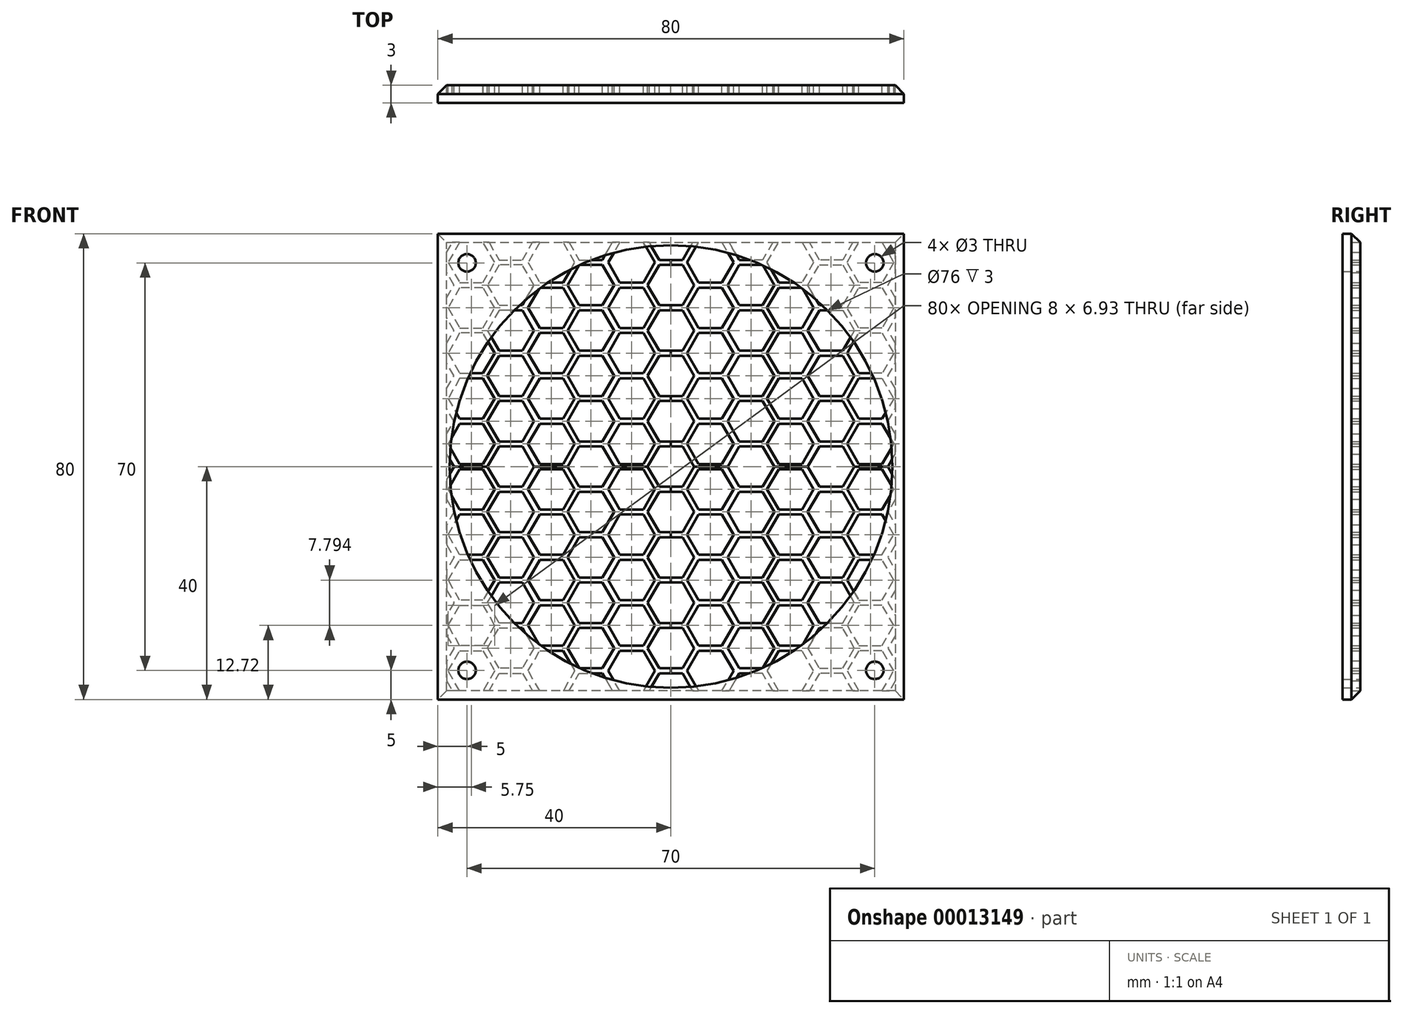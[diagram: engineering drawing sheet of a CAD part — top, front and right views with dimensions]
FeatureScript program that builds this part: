
annotation { "Feature Type Name" : "Feature", "Feature Type Description" : "" }
export const myFeature = defineFeature(function(context is Context, id is Id, definition is map)
    precondition{}
    {
        {
            var Q0;
            Q0=qCreatedBy(makeId("Front.planeOp"),FACE);
            var sketch = newSketch(context, id + "F0", { "sketchPlane" : qUnion([Q0])});
            skLineSegment(sketch, "E0.bottom", {"start": v(-40, 40) * mm, "end": v(40, 40) * mm});
            skLineSegment(sketch, "E0.top", {"start": v(-40, -40) * mm, "end": v(40, -40) * mm});
            skLineSegment(sketch, "E0.left", {"start": v(-40, 40) * mm, "end": v(-40, -40) * mm});
            skLineSegment(sketch, "E0.right", {"start": v(40, 40) * mm, "end": v(40, -40) * mm});
            skCircle(sketch, "E1", {"center": v(0, 0) * mm, "radius": 38 * mm});
            skLineSegment(sketch, "E2.bottom", {"start": v(-35, 35) * mm, "end": v(35, 35) * mm, "construction": true});
            skLineSegment(sketch, "E2.top", {"start": v(-35, -35) * mm, "end": v(35, -35) * mm, "construction": true});
            skLineSegment(sketch, "E2.left", {"start": v(-35, 35) * mm, "end": v(-35, -35) * mm, "construction": true});
            skLineSegment(sketch, "E2.right", {"start": v(35, 35) * mm, "end": v(35, -35) * mm, "construction": true});
            skLineSegment(sketch, "E3", {"start": v(35, 35) * mm, "end": v(-35, -35) * mm, "construction": true});
            skLineSegment(sketch, "E4", {"start": v(-40, 40) * mm, "end": v(40, -40) * mm, "construction": true});
            skCircle(sketch, "E5", {"center": v(35, 35) * mm, "radius": 1.5 * mm});
            skCircle(sketch, "E6", {"center": v(-35, 35) * mm, "radius": 1.5 * mm});
            skCircle(sketch, "E7", {"center": v(35, -35) * mm, "radius": 1.5 * mm});
            skCircle(sketch, "E8", {"center": v(-35, -35) * mm, "radius": 1.5 * mm});
            skSolve(sketch);
        }
        {
            var Q0;
            Q0=makeQuery(id+"F0.imprint","IMPRINT",FACE,{"disambiguationData":[TD([[makeQuery(id+"F0.imprint","IMPRINT",EDGE,{"derivedFrom":sQuery(id+"F0.wireOp",EDGE,"E0.bottom")}),-1.0]])]});
            extrude(context, id + "F1", {"entities" : qUnion([Q0]), "depth" : 3 * mm});
        }
        {
            var Q0;
            Q0=makeQuery(id+"F1.opExtrude","CAP_EDGE",EDGE,{"disambiguationData":[OSD([sQuery(id+"F0.wireOp",EDGE,"E0.bottom")])],"isStart":true});
            var Q1;
            Q1=makeQuery(id+"F1.opExtrude","CAP_EDGE",EDGE,{"disambiguationData":[OSD([sQuery(id+"F0.wireOp",EDGE,"E0.left")])],"isStart":true});
            var Q2;
            Q2=makeQuery(id+"F1.opExtrude","CAP_EDGE",EDGE,{"disambiguationData":[OSD([sQuery(id+"F0.wireOp",EDGE,"E0.top")])],"isStart":true});
            var Q3;
            Q3=makeQuery(id+"F1.opExtrude","CAP_EDGE",EDGE,{"disambiguationData":[OSD([sQuery(id+"F0.wireOp",EDGE,"E0.right")])],"isStart":true});
            chamfer(context, id + "F2", {"entities" : qUnion([Q0, Q1, Q2, Q3]), "width" : 1.5 * mm, "tangentPropagation" : true});
        }
        {
            var Q0;
            Q0=qCreatedBy(makeId("Front.planeOp"),FACE);
            var sketch = newSketch(context, id + "F3", { "sketchPlane" : qUnion([Q0])});
            skCircle(sketch, "E9.cCircle", {"center": v(0, 0) * mm, "radius": 3.46 * mm, "construction": true});
            skLineSegment(sketch, "E9.0", {"start": v(-2, 3.46) * mm, "end": v(2, 3.46) * mm});
            skLineSegment(sketch, "E9.1", {"start": v(2, 3.46) * mm, "end": v(4, 0) * mm});
            skLineSegment(sketch, "E9.2", {"start": v(4, 0) * mm, "end": v(2, -3.46) * mm});
            skLineSegment(sketch, "E9.3", {"start": v(2, -3.46) * mm, "end": v(-2, -3.46) * mm});
            skLineSegment(sketch, "E9.4", {"start": v(-2, -3.46) * mm, "end": v(-4, 0) * mm});
            skLineSegment(sketch, "E9.5", {"start": v(-4, 0) * mm, "end": v(-2, 3.46) * mm});
            skPoint(sketch, "E9.0.midPoint", {"position": v(0, 3.46) * mm});
            skCircle(sketch, "E10.cCircle", {"center": v(6.75, 3.9) * mm, "radius": 3.46 * mm, "construction": true});
            skLineSegment(sketch, "E10.0", {"start": v(4.75, 7.36) * mm, "end": v(8.75, 7.36) * mm});
            skLineSegment(sketch, "E10.1", {"start": v(8.75, 7.36) * mm, "end": v(10.75, 3.9) * mm});
            skLineSegment(sketch, "E10.2", {"start": v(10.75, 3.9) * mm, "end": v(8.75, 0.43) * mm});
            skLineSegment(sketch, "E10.3", {"start": v(8.75, 0.43) * mm, "end": v(4.75, 0.43) * mm});
            skLineSegment(sketch, "E10.4", {"start": v(4.75, 0.43) * mm, "end": v(2.75, 3.9) * mm});
            skLineSegment(sketch, "E10.5", {"start": v(2.75, 3.9) * mm, "end": v(4.75, 7.36) * mm});
            skPoint(sketch, "E10.0.midPoint", {"position": v(6.75, 7.36) * mm});
            skLineSegment(sketch, "E11", {"start": v(0, 0) * mm, "end": v(6.75, 3.9) * mm, "construction": true});
            skLineSegment(sketch, "E12.0.1.0", {"start": v(2, 4.33) * mm, "end": v(-2, 4.33) * mm});
            skLineSegment(sketch, "E12.0.1.1", {"start": v(-2, 4.33) * mm, "end": v(-4, 7.8) * mm});
            skCircle(sketch, "E12.0.1.2", {"center": v(0, 7.8) * mm, "radius": 3.46 * mm, "construction": true});
            skLineSegment(sketch, "E12.0.1.3", {"start": v(4, 7.8) * mm, "end": v(2, 4.33) * mm});
            skLineSegment(sketch, "E12.0.1.4", {"start": v(8.75, 8.23) * mm, "end": v(4.75, 8.23) * mm});
            skLineSegment(sketch, "E12.0.1.5", {"start": v(0, 7.8) * mm, "end": v(6.75, 11.7) * mm, "construction": true});
            skLineSegment(sketch, "E12.0.1.6", {"start": v(-4, 7.8) * mm, "end": v(-2, 11.26) * mm});
            skLineSegment(sketch, "E12.0.1.7", {"start": v(2, 11.26) * mm, "end": v(4, 7.8) * mm});
            skCircle(sketch, "E12.0.1.8", {"center": v(6.75, 11.7) * mm, "radius": 3.46 * mm, "construction": true});
            skPoint(sketch, "E12.0.1.9", {"position": v(0, 11.26) * mm});
            skLineSegment(sketch, "E12.0.1.10", {"start": v(4.75, 8.23) * mm, "end": v(2.75, 11.7) * mm});
            skLineSegment(sketch, "E12.0.1.11", {"start": v(10.75, 11.7) * mm, "end": v(8.75, 8.23) * mm});
            skLineSegment(sketch, "E12.0.1.12", {"start": v(2.75, 11.7) * mm, "end": v(4.75, 15.16) * mm});
            skLineSegment(sketch, "E12.0.1.13", {"start": v(8.75, 15.16) * mm, "end": v(10.75, 11.7) * mm});
            skPoint(sketch, "E12.0.1.14", {"position": v(6.75, 15.16) * mm});
            skLineSegment(sketch, "E12.0.1.15", {"start": v(-2, 11.26) * mm, "end": v(2, 11.26) * mm});
            skLineSegment(sketch, "E12.0.1.16", {"start": v(4.75, 15.16) * mm, "end": v(8.75, 15.16) * mm});
            skLineSegment(sketch, "E12.1.0.0", {"start": v(15.75, -3.46) * mm, "end": v(11.75, -3.46) * mm});
            skLineSegment(sketch, "E12.1.0.1", {"start": v(11.75, -3.46) * mm, "end": v(9.75, 0) * mm});
            skCircle(sketch, "E12.1.0.2", {"center": v(13.75, 0) * mm, "radius": 3.46 * mm, "construction": true});
            skLineSegment(sketch, "E12.1.0.3", {"start": v(17.75, 0) * mm, "end": v(15.75, -3.46) * mm});
            skLineSegment(sketch, "E12.1.0.4", {"start": v(22.5, 0.43) * mm, "end": v(18.5, 0.43) * mm});
            skLineSegment(sketch, "E12.1.0.5", {"start": v(13.75, 0) * mm, "end": v(20.5, 3.9) * mm, "construction": true});
            skLineSegment(sketch, "E12.1.0.6", {"start": v(9.75, 0) * mm, "end": v(11.75, 3.46) * mm});
            skLineSegment(sketch, "E12.1.0.7", {"start": v(15.75, 3.46) * mm, "end": v(17.75, 0) * mm});
            skCircle(sketch, "E12.1.0.8", {"center": v(20.5, 3.9) * mm, "radius": 3.46 * mm, "construction": true});
            skPoint(sketch, "E12.1.0.9", {"position": v(13.75, 3.46) * mm});
            skLineSegment(sketch, "E12.1.0.10", {"start": v(18.5, 0.43) * mm, "end": v(16.5, 3.9) * mm});
            skLineSegment(sketch, "E12.1.0.11", {"start": v(24.5, 3.9) * mm, "end": v(22.5, 0.43) * mm});
            skLineSegment(sketch, "E12.1.0.12", {"start": v(16.5, 3.9) * mm, "end": v(18.5, 7.36) * mm});
            skLineSegment(sketch, "E12.1.0.13", {"start": v(22.5, 7.36) * mm, "end": v(24.5, 3.9) * mm});
            skPoint(sketch, "E12.1.0.14", {"position": v(20.5, 7.36) * mm});
            skLineSegment(sketch, "E12.1.0.15", {"start": v(11.75, 3.46) * mm, "end": v(15.75, 3.46) * mm});
            skLineSegment(sketch, "E12.1.0.16", {"start": v(18.5, 7.36) * mm, "end": v(22.5, 7.36) * mm});
            skLineSegment(sketch, "E12.1.1.0", {"start": v(15.75, 4.33) * mm, "end": v(11.75, 4.33) * mm});
            skLineSegment(sketch, "E12.1.1.1", {"start": v(11.75, 4.33) * mm, "end": v(9.75, 7.8) * mm});
            skCircle(sketch, "E12.1.1.2", {"center": v(13.75, 7.8) * mm, "radius": 3.46 * mm, "construction": true});
            skLineSegment(sketch, "E12.1.1.3", {"start": v(17.75, 7.8) * mm, "end": v(15.75, 4.33) * mm});
            skLineSegment(sketch, "E12.1.1.4", {"start": v(22.5, 8.23) * mm, "end": v(18.5, 8.23) * mm});
            skLineSegment(sketch, "E12.1.1.5", {"start": v(13.75, 7.8) * mm, "end": v(20.5, 11.7) * mm, "construction": true});
            skLineSegment(sketch, "E12.1.1.6", {"start": v(9.75, 7.8) * mm, "end": v(11.75, 11.26) * mm});
            skLineSegment(sketch, "E12.1.1.7", {"start": v(15.75, 11.26) * mm, "end": v(17.75, 7.8) * mm});
            skCircle(sketch, "E12.1.1.8", {"center": v(20.5, 11.7) * mm, "radius": 3.46 * mm, "construction": true});
            skPoint(sketch, "E12.1.1.9", {"position": v(13.75, 11.26) * mm});
            skLineSegment(sketch, "E12.1.1.10", {"start": v(18.5, 8.23) * mm, "end": v(16.5, 11.7) * mm});
            skLineSegment(sketch, "E12.1.1.11", {"start": v(24.5, 11.7) * mm, "end": v(22.5, 8.23) * mm});
            skLineSegment(sketch, "E12.1.1.12", {"start": v(16.5, 11.7) * mm, "end": v(18.5, 15.16) * mm});
            skLineSegment(sketch, "E12.1.1.13", {"start": v(22.5, 15.16) * mm, "end": v(24.5, 11.7) * mm});
            skPoint(sketch, "E12.1.1.14", {"position": v(20.5, 15.16) * mm});
            skLineSegment(sketch, "E12.1.1.15", {"start": v(11.75, 11.26) * mm, "end": v(15.75, 11.26) * mm});
            skLineSegment(sketch, "E12.1.1.16", {"start": v(18.5, 15.16) * mm, "end": v(22.5, 15.16) * mm});
            skLineSegment(sketch, "E12.2.0.0", {"start": v(29.5, -3.46) * mm, "end": v(25.5, -3.46) * mm});
            skLineSegment(sketch, "E12.2.0.1", {"start": v(25.5, -3.46) * mm, "end": v(23.5, 0) * mm});
            skCircle(sketch, "E12.2.0.2", {"center": v(27.5, 0) * mm, "radius": 3.46 * mm, "construction": true});
            skLineSegment(sketch, "E12.2.0.3", {"start": v(31.5, 0) * mm, "end": v(29.5, -3.46) * mm});
            skLineSegment(sketch, "E12.2.0.4", {"start": v(36.25, 0.43) * mm, "end": v(32.25, 0.43) * mm});
            skLineSegment(sketch, "E12.2.0.5", {"start": v(27.5, 0) * mm, "end": v(34.25, 3.9) * mm, "construction": true});
            skLineSegment(sketch, "E12.2.0.6", {"start": v(23.5, 0) * mm, "end": v(25.5, 3.46) * mm});
            skLineSegment(sketch, "E12.2.0.7", {"start": v(29.5, 3.46) * mm, "end": v(31.5, 0) * mm});
            skCircle(sketch, "E12.2.0.8", {"center": v(34.25, 3.9) * mm, "radius": 3.46 * mm, "construction": true});
            skPoint(sketch, "E12.2.0.9", {"position": v(27.5, 3.46) * mm});
            skLineSegment(sketch, "E12.2.0.10", {"start": v(32.25, 0.43) * mm, "end": v(30.25, 3.9) * mm});
            skLineSegment(sketch, "E12.2.0.11", {"start": v(38.25, 3.9) * mm, "end": v(36.25, 0.43) * mm});
            skLineSegment(sketch, "E12.2.0.12", {"start": v(30.25, 3.9) * mm, "end": v(32.25, 7.36) * mm});
            skLineSegment(sketch, "E12.2.0.13", {"start": v(36.25, 7.36) * mm, "end": v(38.25, 3.9) * mm});
            skPoint(sketch, "E12.2.0.14", {"position": v(34.25, 7.36) * mm});
            skLineSegment(sketch, "E12.2.0.15", {"start": v(25.5, 3.46) * mm, "end": v(29.5, 3.46) * mm});
            skLineSegment(sketch, "E12.2.0.16", {"start": v(32.25, 7.36) * mm, "end": v(36.25, 7.36) * mm});
            skLineSegment(sketch, "E12.2.1.0", {"start": v(29.5, 4.33) * mm, "end": v(25.5, 4.33) * mm});
            skLineSegment(sketch, "E12.2.1.1", {"start": v(25.5, 4.33) * mm, "end": v(23.5, 7.8) * mm});
            skCircle(sketch, "E12.2.1.2", {"center": v(27.5, 7.8) * mm, "radius": 3.46 * mm, "construction": true});
            skLineSegment(sketch, "E12.2.1.3", {"start": v(31.5, 7.8) * mm, "end": v(29.5, 4.33) * mm});
            skLineSegment(sketch, "E12.2.1.4", {"start": v(36.25, 8.23) * mm, "end": v(32.25, 8.23) * mm});
            skLineSegment(sketch, "E12.2.1.5", {"start": v(27.5, 7.8) * mm, "end": v(34.25, 11.7) * mm, "construction": true});
            skLineSegment(sketch, "E12.2.1.6", {"start": v(23.5, 7.8) * mm, "end": v(25.5, 11.26) * mm});
            skLineSegment(sketch, "E12.2.1.7", {"start": v(29.5, 11.26) * mm, "end": v(31.5, 7.8) * mm});
            skCircle(sketch, "E12.2.1.8", {"center": v(34.25, 11.7) * mm, "radius": 3.46 * mm, "construction": true});
            skPoint(sketch, "E12.2.1.9", {"position": v(27.5, 11.26) * mm});
            skLineSegment(sketch, "E12.2.1.10", {"start": v(32.25, 8.23) * mm, "end": v(30.25, 11.7) * mm});
            skLineSegment(sketch, "E12.2.1.11", {"start": v(38.25, 11.7) * mm, "end": v(36.25, 8.23) * mm});
            skLineSegment(sketch, "E12.2.1.12", {"start": v(30.25, 11.7) * mm, "end": v(32.25, 15.16) * mm});
            skLineSegment(sketch, "E12.2.1.13", {"start": v(36.25, 15.16) * mm, "end": v(38.25, 11.7) * mm});
            skPoint(sketch, "E12.2.1.14", {"position": v(34.25, 15.16) * mm});
            skLineSegment(sketch, "E12.2.1.15", {"start": v(25.5, 11.26) * mm, "end": v(29.5, 11.26) * mm});
            skLineSegment(sketch, "E12.2.1.16", {"start": v(32.25, 15.16) * mm, "end": v(36.25, 15.16) * mm});
            skLineSegment(sketch, "E12.direction1", {"start": v(-2, -3.46) * mm, "end": v(11.75, -3.46) * mm, "construction": true});
            skLineSegment(sketch, "E12.direction2", {"start": v(-2, -3.46) * mm, "end": v(-2, 4.33) * mm, "construction": true});
            skLineSegment(sketch, "E13", {"start": v(0, 35) * mm, "end": v(0, 0) * mm});
            skLineSegment(sketch, "E14.0.0.2", {"start": v(2, 12.12) * mm, "end": v(-2, 12.12) * mm});
            skLineSegment(sketch, "E14.3.0.2", {"start": v(-2, 12.12) * mm, "end": v(-4, 15.59) * mm});
            skCircle(sketch, "E14.6.0.2", {"center": v(0, 15.59) * mm, "radius": 3.46 * mm, "construction": true});
            skLineSegment(sketch, "E14.8.0.2", {"start": v(4, 15.59) * mm, "end": v(2, 12.12) * mm});
            skLineSegment(sketch, "E14.11.0.2", {"start": v(8.75, 16.02) * mm, "end": v(4.75, 16.02) * mm});
            skLineSegment(sketch, "E14.14.0.2", {"start": v(0, 15.59) * mm, "end": v(6.75, 19.49) * mm, "construction": true});
            skLineSegment(sketch, "E14.17.0.2", {"start": v(-4, 15.59) * mm, "end": v(-2, 19.05) * mm});
            skLineSegment(sketch, "E14.20.0.2", {"start": v(2, 19.05) * mm, "end": v(4, 15.59) * mm});
            skCircle(sketch, "E14.23.0.2", {"center": v(6.75, 19.49) * mm, "radius": 3.46 * mm, "construction": true});
            skPoint(sketch, "E14.25.0.2", {"position": v(0, 19.05) * mm});
            skLineSegment(sketch, "E14.26.0.2", {"start": v(4.75, 16.02) * mm, "end": v(2.75, 19.49) * mm});
            skLineSegment(sketch, "E14.29.0.2", {"start": v(10.75, 19.49) * mm, "end": v(8.75, 16.02) * mm});
            skLineSegment(sketch, "E14.32.0.2", {"start": v(2.75, 19.49) * mm, "end": v(4.75, 22.95) * mm});
            skLineSegment(sketch, "E14.35.0.2", {"start": v(8.75, 22.95) * mm, "end": v(10.75, 19.49) * mm});
            skPoint(sketch, "E14.38.0.2", {"position": v(6.75, 22.95) * mm});
            skLineSegment(sketch, "E14.39.0.2", {"start": v(-2, 19.05) * mm, "end": v(2, 19.05) * mm});
            skLineSegment(sketch, "E14.42.0.2", {"start": v(4.75, 22.95) * mm, "end": v(8.75, 22.95) * mm});
            skLineSegment(sketch, "E14.0.0.3", {"start": v(2, 19.92) * mm, "end": v(-2, 19.92) * mm});
            skLineSegment(sketch, "E14.3.0.3", {"start": v(-2, 19.92) * mm, "end": v(-4, 23.38) * mm});
            skCircle(sketch, "E14.6.0.3", {"center": v(0, 23.38) * mm, "radius": 3.46 * mm, "construction": true});
            skLineSegment(sketch, "E14.8.0.3", {"start": v(4, 23.38) * mm, "end": v(2, 19.92) * mm});
            skLineSegment(sketch, "E14.11.0.3", {"start": v(8.75, 23.82) * mm, "end": v(4.75, 23.82) * mm});
            skLineSegment(sketch, "E14.14.0.3", {"start": v(0, 23.38) * mm, "end": v(6.75, 27.28) * mm, "construction": true});
            skLineSegment(sketch, "E14.17.0.3", {"start": v(-4, 23.38) * mm, "end": v(-2, 26.85) * mm});
            skLineSegment(sketch, "E14.20.0.3", {"start": v(2, 26.85) * mm, "end": v(4, 23.38) * mm});
            skCircle(sketch, "E14.23.0.3", {"center": v(6.75, 27.28) * mm, "radius": 3.46 * mm, "construction": true});
            skPoint(sketch, "E14.25.0.3", {"position": v(0, 26.85) * mm});
            skLineSegment(sketch, "E14.26.0.3", {"start": v(4.75, 23.82) * mm, "end": v(2.75, 27.28) * mm});
            skLineSegment(sketch, "E14.29.0.3", {"start": v(10.75, 27.28) * mm, "end": v(8.75, 23.82) * mm});
            skLineSegment(sketch, "E14.32.0.3", {"start": v(2.75, 27.28) * mm, "end": v(4.75, 30.74) * mm});
            skLineSegment(sketch, "E14.35.0.3", {"start": v(8.75, 30.74) * mm, "end": v(10.75, 27.28) * mm});
            skPoint(sketch, "E14.38.0.3", {"position": v(6.75, 30.74) * mm});
            skLineSegment(sketch, "E14.39.0.3", {"start": v(-2, 26.85) * mm, "end": v(2, 26.85) * mm});
            skLineSegment(sketch, "E14.42.0.3", {"start": v(4.75, 30.74) * mm, "end": v(8.75, 30.74) * mm});
            skLineSegment(sketch, "E14.0.1.2", {"start": v(15.75, 12.12) * mm, "end": v(11.75, 12.12) * mm});
            skLineSegment(sketch, "E14.3.1.2", {"start": v(11.75, 12.12) * mm, "end": v(9.75, 15.59) * mm});
            skCircle(sketch, "E14.6.1.2", {"center": v(13.75, 15.59) * mm, "radius": 3.46 * mm, "construction": true});
            skLineSegment(sketch, "E14.8.1.2", {"start": v(17.75, 15.59) * mm, "end": v(15.75, 12.12) * mm});
            skLineSegment(sketch, "E14.11.1.2", {"start": v(22.5, 16.02) * mm, "end": v(18.5, 16.02) * mm});
            skLineSegment(sketch, "E14.14.1.2", {"start": v(13.75, 15.59) * mm, "end": v(20.5, 19.49) * mm, "construction": true});
            skLineSegment(sketch, "E14.17.1.2", {"start": v(9.75, 15.59) * mm, "end": v(11.75, 19.05) * mm});
            skLineSegment(sketch, "E14.20.1.2", {"start": v(15.75, 19.05) * mm, "end": v(17.75, 15.59) * mm});
            skCircle(sketch, "E14.23.1.2", {"center": v(20.5, 19.49) * mm, "radius": 3.46 * mm, "construction": true});
            skPoint(sketch, "E14.25.1.2", {"position": v(13.75, 19.05) * mm});
            skLineSegment(sketch, "E14.26.1.2", {"start": v(18.5, 16.02) * mm, "end": v(16.5, 19.49) * mm});
            skLineSegment(sketch, "E14.29.1.2", {"start": v(24.5, 19.49) * mm, "end": v(22.5, 16.02) * mm});
            skLineSegment(sketch, "E14.32.1.2", {"start": v(16.5, 19.49) * mm, "end": v(18.5, 22.95) * mm});
            skLineSegment(sketch, "E14.35.1.2", {"start": v(22.5, 22.95) * mm, "end": v(24.5, 19.49) * mm});
            skPoint(sketch, "E14.38.1.2", {"position": v(20.5, 22.95) * mm});
            skLineSegment(sketch, "E14.39.1.2", {"start": v(11.75, 19.05) * mm, "end": v(15.75, 19.05) * mm});
            skLineSegment(sketch, "E14.42.1.2", {"start": v(18.5, 22.95) * mm, "end": v(22.5, 22.95) * mm});
            skLineSegment(sketch, "E14.0.1.3", {"start": v(15.75, 19.92) * mm, "end": v(11.75, 19.92) * mm});
            skLineSegment(sketch, "E14.3.1.3", {"start": v(11.75, 19.92) * mm, "end": v(9.75, 23.38) * mm});
            skCircle(sketch, "E14.6.1.3", {"center": v(13.75, 23.38) * mm, "radius": 3.46 * mm, "construction": true});
            skLineSegment(sketch, "E14.8.1.3", {"start": v(17.75, 23.38) * mm, "end": v(15.75, 19.92) * mm});
            skLineSegment(sketch, "E14.11.1.3", {"start": v(22.5, 23.82) * mm, "end": v(18.5, 23.82) * mm});
            skLineSegment(sketch, "E14.14.1.3", {"start": v(13.75, 23.38) * mm, "end": v(20.5, 27.28) * mm, "construction": true});
            skLineSegment(sketch, "E14.17.1.3", {"start": v(9.75, 23.38) * mm, "end": v(11.75, 26.85) * mm});
            skLineSegment(sketch, "E14.20.1.3", {"start": v(15.75, 26.85) * mm, "end": v(17.75, 23.38) * mm});
            skCircle(sketch, "E14.23.1.3", {"center": v(20.5, 27.28) * mm, "radius": 3.46 * mm, "construction": true});
            skPoint(sketch, "E14.25.1.3", {"position": v(13.75, 26.85) * mm});
            skLineSegment(sketch, "E14.26.1.3", {"start": v(18.5, 23.82) * mm, "end": v(16.5, 27.28) * mm});
            skLineSegment(sketch, "E14.29.1.3", {"start": v(24.5, 27.28) * mm, "end": v(22.5, 23.82) * mm});
            skLineSegment(sketch, "E14.32.1.3", {"start": v(16.5, 27.28) * mm, "end": v(18.5, 30.74) * mm});
            skLineSegment(sketch, "E14.35.1.3", {"start": v(22.5, 30.74) * mm, "end": v(24.5, 27.28) * mm});
            skPoint(sketch, "E14.38.1.3", {"position": v(20.5, 30.74) * mm});
            skLineSegment(sketch, "E14.39.1.3", {"start": v(11.75, 26.85) * mm, "end": v(15.75, 26.85) * mm});
            skLineSegment(sketch, "E14.42.1.3", {"start": v(18.5, 30.74) * mm, "end": v(22.5, 30.74) * mm});
            skLineSegment(sketch, "E14.0.2.2", {"start": v(29.5, 12.12) * mm, "end": v(25.5, 12.12) * mm});
            skLineSegment(sketch, "E14.3.2.2", {"start": v(25.5, 12.12) * mm, "end": v(23.5, 15.59) * mm});
            skCircle(sketch, "E14.6.2.2", {"center": v(27.5, 15.59) * mm, "radius": 3.46 * mm, "construction": true});
            skLineSegment(sketch, "E14.8.2.2", {"start": v(31.5, 15.59) * mm, "end": v(29.5, 12.12) * mm});
            skLineSegment(sketch, "E14.11.2.2", {"start": v(36.25, 16.02) * mm, "end": v(32.25, 16.02) * mm});
            skLineSegment(sketch, "E14.14.2.2", {"start": v(27.5, 15.59) * mm, "end": v(34.25, 19.49) * mm, "construction": true});
            skLineSegment(sketch, "E14.17.2.2", {"start": v(23.5, 15.59) * mm, "end": v(25.5, 19.05) * mm});
            skLineSegment(sketch, "E14.20.2.2", {"start": v(29.5, 19.05) * mm, "end": v(31.5, 15.59) * mm});
            skCircle(sketch, "E14.23.2.2", {"center": v(34.25, 19.49) * mm, "radius": 3.46 * mm, "construction": true});
            skPoint(sketch, "E14.25.2.2", {"position": v(27.5, 19.05) * mm});
            skLineSegment(sketch, "E14.26.2.2", {"start": v(32.25, 16.02) * mm, "end": v(30.25, 19.49) * mm});
            skLineSegment(sketch, "E14.29.2.2", {"start": v(38.25, 19.49) * mm, "end": v(36.25, 16.02) * mm});
            skLineSegment(sketch, "E14.32.2.2", {"start": v(30.25, 19.49) * mm, "end": v(32.25, 22.95) * mm});
            skLineSegment(sketch, "E14.35.2.2", {"start": v(36.25, 22.95) * mm, "end": v(38.25, 19.49) * mm});
            skPoint(sketch, "E14.38.2.2", {"position": v(34.25, 22.95) * mm});
            skLineSegment(sketch, "E14.39.2.2", {"start": v(25.5, 19.05) * mm, "end": v(29.5, 19.05) * mm});
            skLineSegment(sketch, "E14.42.2.2", {"start": v(32.25, 22.95) * mm, "end": v(36.25, 22.95) * mm});
            skLineSegment(sketch, "E14.0.2.3", {"start": v(29.5, 19.92) * mm, "end": v(25.5, 19.92) * mm});
            skLineSegment(sketch, "E14.3.2.3", {"start": v(25.5, 19.92) * mm, "end": v(23.5, 23.38) * mm});
            skCircle(sketch, "E14.6.2.3", {"center": v(27.5, 23.38) * mm, "radius": 3.46 * mm, "construction": true});
            skLineSegment(sketch, "E14.8.2.3", {"start": v(31.5, 23.38) * mm, "end": v(29.5, 19.92) * mm});
            skLineSegment(sketch, "E14.11.2.3", {"start": v(36.25, 23.82) * mm, "end": v(32.25, 23.82) * mm});
            skLineSegment(sketch, "E14.14.2.3", {"start": v(27.5, 23.38) * mm, "end": v(34.25, 27.28) * mm, "construction": true});
            skLineSegment(sketch, "E14.17.2.3", {"start": v(23.5, 23.38) * mm, "end": v(25.5, 26.85) * mm});
            skLineSegment(sketch, "E14.20.2.3", {"start": v(29.5, 26.85) * mm, "end": v(31.5, 23.38) * mm});
            skCircle(sketch, "E14.23.2.3", {"center": v(34.25, 27.28) * mm, "radius": 3.46 * mm, "construction": true});
            skPoint(sketch, "E14.25.2.3", {"position": v(27.5, 26.85) * mm});
            skLineSegment(sketch, "E14.26.2.3", {"start": v(32.25, 23.82) * mm, "end": v(30.25, 27.28) * mm});
            skLineSegment(sketch, "E14.29.2.3", {"start": v(38.25, 27.28) * mm, "end": v(36.25, 23.82) * mm});
            skLineSegment(sketch, "E14.32.2.3", {"start": v(30.25, 27.28) * mm, "end": v(32.25, 30.74) * mm});
            skLineSegment(sketch, "E14.35.2.3", {"start": v(36.25, 30.74) * mm, "end": v(38.25, 27.28) * mm});
            skPoint(sketch, "E14.38.2.3", {"position": v(34.25, 30.74) * mm});
            skLineSegment(sketch, "E14.39.2.3", {"start": v(25.5, 26.85) * mm, "end": v(29.5, 26.85) * mm});
            skLineSegment(sketch, "E14.42.2.3", {"start": v(32.25, 30.74) * mm, "end": v(36.25, 30.74) * mm});
            skLineSegment(sketch, "E15.0.0.4", {"start": v(2, 27.71) * mm, "end": v(-2, 27.71) * mm});
            skLineSegment(sketch, "E15.3.0.4", {"start": v(-2, 27.71) * mm, "end": v(-4, 31.18) * mm});
            skCircle(sketch, "E15.6.0.4", {"center": v(0, 31.18) * mm, "radius": 3.46 * mm, "construction": true});
            skLineSegment(sketch, "E15.8.0.4", {"start": v(4, 31.18) * mm, "end": v(2, 27.71) * mm});
            skLineSegment(sketch, "E15.11.0.4", {"start": v(8.75, 31.6) * mm, "end": v(4.75, 31.6) * mm});
            skLineSegment(sketch, "E15.14.0.4", {"start": v(0, 31.18) * mm, "end": v(6.75, 35.07) * mm, "construction": true});
            skLineSegment(sketch, "E15.17.0.4", {"start": v(-4, 31.18) * mm, "end": v(-2, 34.64) * mm});
            skLineSegment(sketch, "E15.20.0.4", {"start": v(2, 34.64) * mm, "end": v(4, 31.18) * mm});
            skCircle(sketch, "E15.23.0.4", {"center": v(6.75, 35.07) * mm, "radius": 3.46 * mm, "construction": true});
            skPoint(sketch, "E15.25.0.4", {"position": v(0, 34.64) * mm});
            skLineSegment(sketch, "E15.26.0.4", {"start": v(4.75, 31.6) * mm, "end": v(2.75, 35.07) * mm});
            skLineSegment(sketch, "E15.29.0.4", {"start": v(10.75, 35.07) * mm, "end": v(8.75, 31.6) * mm});
            skLineSegment(sketch, "E15.32.0.4", {"start": v(2.75, 35.07) * mm, "end": v(4.75, 38.54) * mm});
            skLineSegment(sketch, "E15.35.0.4", {"start": v(8.75, 38.54) * mm, "end": v(10.75, 35.07) * mm});
            skPoint(sketch, "E15.38.0.4", {"position": v(6.75, 38.54) * mm});
            skLineSegment(sketch, "E15.39.0.4", {"start": v(-2, 34.64) * mm, "end": v(2, 34.64) * mm});
            skLineSegment(sketch, "E15.42.0.4", {"start": v(4.75, 38.54) * mm, "end": v(8.75, 38.54) * mm});
            skLineSegment(sketch, "E15.0.1.4", {"start": v(15.75, 27.71) * mm, "end": v(11.75, 27.71) * mm});
            skLineSegment(sketch, "E15.3.1.4", {"start": v(11.75, 27.71) * mm, "end": v(9.75, 31.18) * mm});
            skCircle(sketch, "E15.6.1.4", {"center": v(13.75, 31.18) * mm, "radius": 3.46 * mm, "construction": true});
            skLineSegment(sketch, "E15.8.1.4", {"start": v(17.75, 31.18) * mm, "end": v(15.75, 27.71) * mm});
            skLineSegment(sketch, "E15.11.1.4", {"start": v(22.5, 31.6) * mm, "end": v(18.5, 31.6) * mm});
            skLineSegment(sketch, "E15.14.1.4", {"start": v(13.75, 31.18) * mm, "end": v(20.5, 35.07) * mm, "construction": true});
            skLineSegment(sketch, "E15.17.1.4", {"start": v(9.75, 31.18) * mm, "end": v(11.75, 34.64) * mm});
            skLineSegment(sketch, "E15.20.1.4", {"start": v(15.75, 34.64) * mm, "end": v(17.75, 31.18) * mm});
            skCircle(sketch, "E15.23.1.4", {"center": v(20.5, 35.07) * mm, "radius": 3.46 * mm, "construction": true});
            skPoint(sketch, "E15.25.1.4", {"position": v(13.75, 34.64) * mm});
            skLineSegment(sketch, "E15.26.1.4", {"start": v(18.5, 31.6) * mm, "end": v(16.5, 35.07) * mm});
            skLineSegment(sketch, "E15.29.1.4", {"start": v(24.5, 35.07) * mm, "end": v(22.5, 31.6) * mm});
            skLineSegment(sketch, "E15.32.1.4", {"start": v(16.5, 35.07) * mm, "end": v(18.5, 38.54) * mm});
            skLineSegment(sketch, "E15.35.1.4", {"start": v(22.5, 38.54) * mm, "end": v(24.5, 35.07) * mm});
            skPoint(sketch, "E15.38.1.4", {"position": v(20.5, 38.54) * mm});
            skLineSegment(sketch, "E15.39.1.4", {"start": v(11.75, 34.64) * mm, "end": v(15.75, 34.64) * mm});
            skLineSegment(sketch, "E15.42.1.4", {"start": v(18.5, 38.54) * mm, "end": v(22.5, 38.54) * mm});
            skLineSegment(sketch, "E15.0.2.4", {"start": v(29.5, 27.71) * mm, "end": v(25.5, 27.71) * mm});
            skLineSegment(sketch, "E15.3.2.4", {"start": v(25.5, 27.71) * mm, "end": v(23.5, 31.18) * mm});
            skCircle(sketch, "E15.6.2.4", {"center": v(27.5, 31.18) * mm, "radius": 3.46 * mm, "construction": true});
            skLineSegment(sketch, "E15.8.2.4", {"start": v(31.5, 31.18) * mm, "end": v(29.5, 27.71) * mm});
            skLineSegment(sketch, "E15.11.2.4", {"start": v(36.25, 31.6) * mm, "end": v(32.25, 31.6) * mm});
            skLineSegment(sketch, "E15.14.2.4", {"start": v(27.5, 31.18) * mm, "end": v(34.25, 35.07) * mm, "construction": true});
            skLineSegment(sketch, "E15.17.2.4", {"start": v(23.5, 31.18) * mm, "end": v(25.5, 34.64) * mm});
            skLineSegment(sketch, "E15.20.2.4", {"start": v(29.5, 34.64) * mm, "end": v(31.5, 31.18) * mm});
            skCircle(sketch, "E15.23.2.4", {"center": v(34.25, 35.07) * mm, "radius": 3.46 * mm, "construction": true});
            skPoint(sketch, "E15.25.2.4", {"position": v(27.5, 34.64) * mm});
            skLineSegment(sketch, "E15.26.2.4", {"start": v(32.25, 31.6) * mm, "end": v(30.25, 35.07) * mm});
            skLineSegment(sketch, "E15.29.2.4", {"start": v(38.25, 35.07) * mm, "end": v(36.25, 31.6) * mm});
            skLineSegment(sketch, "E15.32.2.4", {"start": v(30.25, 35.07) * mm, "end": v(32.25, 38.54) * mm});
            skLineSegment(sketch, "E15.35.2.4", {"start": v(36.25, 38.54) * mm, "end": v(38.25, 35.07) * mm});
            skPoint(sketch, "E15.38.2.4", {"position": v(34.25, 38.54) * mm});
            skLineSegment(sketch, "E15.39.2.4", {"start": v(25.5, 34.64) * mm, "end": v(29.5, 34.64) * mm});
            skLineSegment(sketch, "E15.42.2.4", {"start": v(32.25, 38.54) * mm, "end": v(36.25, 38.54) * mm});
            skLineSegment(sketch, "E16.bottom", {"start": v(0, 0) * mm, "end": v(38.5, 0) * mm});
            skLineSegment(sketch, "E16.top", {"start": v(0, 38.5) * mm, "end": v(38.5, 38.5) * mm});
            skLineSegment(sketch, "E16.left", {"start": v(0, 0) * mm, "end": v(0, 38.5) * mm});
            skLineSegment(sketch, "E16.right", {"start": v(38.5, 0) * mm, "end": v(38.5, 38.5) * mm});
            skLineSegment(sketch, "E17.0.3.0", {"start": v(43.25, -3.46) * mm, "end": v(39.25, -3.46) * mm});
            skLineSegment(sketch, "E17.3.3.0", {"start": v(39.25, -3.46) * mm, "end": v(37.25, 0) * mm});
            skCircle(sketch, "E17.6.3.0", {"center": v(41.25, 0) * mm, "radius": 3.46 * mm, "construction": true});
            skLineSegment(sketch, "E17.8.3.0", {"start": v(45.25, 0) * mm, "end": v(43.25, -3.46) * mm});
            skLineSegment(sketch, "E17.11.3.0", {"start": v(50, 0.43) * mm, "end": v(46, 0.43) * mm});
            skLineSegment(sketch, "E17.14.3.0", {"start": v(41.25, 0) * mm, "end": v(48, 3.9) * mm, "construction": true});
            skLineSegment(sketch, "E17.17.3.0", {"start": v(37.25, 0) * mm, "end": v(39.25, 3.46) * mm});
            skLineSegment(sketch, "E17.20.3.0", {"start": v(43.25, 3.46) * mm, "end": v(45.25, 0) * mm});
            skCircle(sketch, "E17.23.3.0", {"center": v(48, 3.9) * mm, "radius": 3.46 * mm, "construction": true});
            skPoint(sketch, "E17.25.3.0", {"position": v(41.25, 3.46) * mm});
            skLineSegment(sketch, "E17.26.3.0", {"start": v(46, 0.43) * mm, "end": v(44, 3.9) * mm});
            skLineSegment(sketch, "E17.29.3.0", {"start": v(52, 3.9) * mm, "end": v(50, 0.43) * mm});
            skLineSegment(sketch, "E17.32.3.0", {"start": v(44, 3.9) * mm, "end": v(46, 7.36) * mm});
            skLineSegment(sketch, "E17.35.3.0", {"start": v(50, 7.36) * mm, "end": v(52, 3.9) * mm});
            skPoint(sketch, "E17.38.3.0", {"position": v(48, 7.36) * mm});
            skLineSegment(sketch, "E17.39.3.0", {"start": v(39.25, 3.46) * mm, "end": v(43.25, 3.46) * mm});
            skLineSegment(sketch, "E17.42.3.0", {"start": v(46, 7.36) * mm, "end": v(50, 7.36) * mm});
            skLineSegment(sketch, "E17.0.3.1", {"start": v(43.25, 4.33) * mm, "end": v(39.25, 4.33) * mm});
            skLineSegment(sketch, "E17.3.3.1", {"start": v(39.25, 4.33) * mm, "end": v(37.25, 7.8) * mm});
            skCircle(sketch, "E17.6.3.1", {"center": v(41.25, 7.8) * mm, "radius": 3.46 * mm, "construction": true});
            skLineSegment(sketch, "E17.8.3.1", {"start": v(45.25, 7.8) * mm, "end": v(43.25, 4.33) * mm});
            skLineSegment(sketch, "E17.11.3.1", {"start": v(50, 8.23) * mm, "end": v(46, 8.23) * mm});
            skLineSegment(sketch, "E17.14.3.1", {"start": v(41.25, 7.8) * mm, "end": v(48, 11.7) * mm, "construction": true});
            skLineSegment(sketch, "E17.17.3.1", {"start": v(37.25, 7.8) * mm, "end": v(39.25, 11.26) * mm});
            skLineSegment(sketch, "E17.20.3.1", {"start": v(43.25, 11.26) * mm, "end": v(45.25, 7.8) * mm});
            skCircle(sketch, "E17.23.3.1", {"center": v(48, 11.7) * mm, "radius": 3.46 * mm, "construction": true});
            skPoint(sketch, "E17.25.3.1", {"position": v(41.25, 11.26) * mm});
            skLineSegment(sketch, "E17.26.3.1", {"start": v(46, 8.23) * mm, "end": v(44, 11.7) * mm});
            skLineSegment(sketch, "E17.29.3.1", {"start": v(52, 11.7) * mm, "end": v(50, 8.23) * mm});
            skLineSegment(sketch, "E17.32.3.1", {"start": v(44, 11.7) * mm, "end": v(46, 15.16) * mm});
            skLineSegment(sketch, "E17.35.3.1", {"start": v(50, 15.16) * mm, "end": v(52, 11.7) * mm});
            skPoint(sketch, "E17.38.3.1", {"position": v(48, 15.16) * mm});
            skLineSegment(sketch, "E17.39.3.1", {"start": v(39.25, 11.26) * mm, "end": v(43.25, 11.26) * mm});
            skLineSegment(sketch, "E17.42.3.1", {"start": v(46, 15.16) * mm, "end": v(50, 15.16) * mm});
            skLineSegment(sketch, "E17.0.3.2", {"start": v(43.25, 12.12) * mm, "end": v(39.25, 12.12) * mm});
            skLineSegment(sketch, "E17.3.3.2", {"start": v(39.25, 12.12) * mm, "end": v(37.25, 15.59) * mm});
            skCircle(sketch, "E17.6.3.2", {"center": v(41.25, 15.59) * mm, "radius": 3.46 * mm, "construction": true});
            skLineSegment(sketch, "E17.8.3.2", {"start": v(45.25, 15.59) * mm, "end": v(43.25, 12.12) * mm});
            skLineSegment(sketch, "E17.11.3.2", {"start": v(50, 16.02) * mm, "end": v(46, 16.02) * mm});
            skLineSegment(sketch, "E17.14.3.2", {"start": v(41.25, 15.59) * mm, "end": v(48, 19.49) * mm, "construction": true});
            skLineSegment(sketch, "E17.17.3.2", {"start": v(37.25, 15.59) * mm, "end": v(39.25, 19.05) * mm});
            skLineSegment(sketch, "E17.20.3.2", {"start": v(43.25, 19.05) * mm, "end": v(45.25, 15.59) * mm});
            skCircle(sketch, "E17.23.3.2", {"center": v(48, 19.49) * mm, "radius": 3.46 * mm, "construction": true});
            skPoint(sketch, "E17.25.3.2", {"position": v(41.25, 19.05) * mm});
            skLineSegment(sketch, "E17.26.3.2", {"start": v(46, 16.02) * mm, "end": v(44, 19.49) * mm});
            skLineSegment(sketch, "E17.29.3.2", {"start": v(52, 19.49) * mm, "end": v(50, 16.02) * mm});
            skLineSegment(sketch, "E17.32.3.2", {"start": v(44, 19.49) * mm, "end": v(46, 22.95) * mm});
            skLineSegment(sketch, "E17.35.3.2", {"start": v(50, 22.95) * mm, "end": v(52, 19.49) * mm});
            skPoint(sketch, "E17.38.3.2", {"position": v(48, 22.95) * mm});
            skLineSegment(sketch, "E17.39.3.2", {"start": v(39.25, 19.05) * mm, "end": v(43.25, 19.05) * mm});
            skLineSegment(sketch, "E17.42.3.2", {"start": v(46, 22.95) * mm, "end": v(50, 22.95) * mm});
            skLineSegment(sketch, "E17.0.3.3", {"start": v(43.25, 19.92) * mm, "end": v(39.25, 19.92) * mm});
            skLineSegment(sketch, "E17.3.3.3", {"start": v(39.25, 19.92) * mm, "end": v(37.25, 23.38) * mm});
            skCircle(sketch, "E17.6.3.3", {"center": v(41.25, 23.38) * mm, "radius": 3.46 * mm, "construction": true});
            skLineSegment(sketch, "E17.8.3.3", {"start": v(45.25, 23.38) * mm, "end": v(43.25, 19.92) * mm});
            skLineSegment(sketch, "E17.11.3.3", {"start": v(50, 23.82) * mm, "end": v(46, 23.82) * mm});
            skLineSegment(sketch, "E17.14.3.3", {"start": v(41.25, 23.38) * mm, "end": v(48, 27.28) * mm, "construction": true});
            skLineSegment(sketch, "E17.17.3.3", {"start": v(37.25, 23.38) * mm, "end": v(39.25, 26.85) * mm});
            skLineSegment(sketch, "E17.20.3.3", {"start": v(43.25, 26.85) * mm, "end": v(45.25, 23.38) * mm});
            skCircle(sketch, "E17.23.3.3", {"center": v(48, 27.28) * mm, "radius": 3.46 * mm, "construction": true});
            skPoint(sketch, "E17.25.3.3", {"position": v(41.25, 26.85) * mm});
            skLineSegment(sketch, "E17.26.3.3", {"start": v(46, 23.82) * mm, "end": v(44, 27.28) * mm});
            skLineSegment(sketch, "E17.29.3.3", {"start": v(52, 27.28) * mm, "end": v(50, 23.82) * mm});
            skLineSegment(sketch, "E17.32.3.3", {"start": v(44, 27.28) * mm, "end": v(46, 30.74) * mm});
            skLineSegment(sketch, "E17.35.3.3", {"start": v(50, 30.74) * mm, "end": v(52, 27.28) * mm});
            skPoint(sketch, "E17.38.3.3", {"position": v(48, 30.74) * mm});
            skLineSegment(sketch, "E17.39.3.3", {"start": v(39.25, 26.85) * mm, "end": v(43.25, 26.85) * mm});
            skLineSegment(sketch, "E17.42.3.3", {"start": v(46, 30.74) * mm, "end": v(50, 30.74) * mm});
            skLineSegment(sketch, "E17.0.3.4", {"start": v(43.25, 27.71) * mm, "end": v(39.25, 27.71) * mm});
            skLineSegment(sketch, "E17.3.3.4", {"start": v(39.25, 27.71) * mm, "end": v(37.25, 31.18) * mm});
            skCircle(sketch, "E17.6.3.4", {"center": v(41.25, 31.18) * mm, "radius": 3.46 * mm, "construction": true});
            skLineSegment(sketch, "E17.8.3.4", {"start": v(45.25, 31.18) * mm, "end": v(43.25, 27.71) * mm});
            skLineSegment(sketch, "E17.11.3.4", {"start": v(50, 31.6) * mm, "end": v(46, 31.6) * mm});
            skLineSegment(sketch, "E17.14.3.4", {"start": v(41.25, 31.18) * mm, "end": v(48, 35.07) * mm, "construction": true});
            skLineSegment(sketch, "E17.17.3.4", {"start": v(37.25, 31.18) * mm, "end": v(39.25, 34.64) * mm});
            skLineSegment(sketch, "E17.20.3.4", {"start": v(43.25, 34.64) * mm, "end": v(45.25, 31.18) * mm});
            skCircle(sketch, "E17.23.3.4", {"center": v(48, 35.07) * mm, "radius": 3.46 * mm, "construction": true});
            skPoint(sketch, "E17.25.3.4", {"position": v(41.25, 34.64) * mm});
            skLineSegment(sketch, "E17.26.3.4", {"start": v(46, 31.6) * mm, "end": v(44, 35.07) * mm});
            skLineSegment(sketch, "E17.29.3.4", {"start": v(52, 35.07) * mm, "end": v(50, 31.6) * mm});
            skLineSegment(sketch, "E17.32.3.4", {"start": v(44, 35.07) * mm, "end": v(46, 38.54) * mm});
            skLineSegment(sketch, "E17.35.3.4", {"start": v(50, 38.54) * mm, "end": v(52, 35.07) * mm});
            skPoint(sketch, "E17.38.3.4", {"position": v(48, 38.54) * mm});
            skLineSegment(sketch, "E17.39.3.4", {"start": v(39.25, 34.64) * mm, "end": v(43.25, 34.64) * mm});
            skLineSegment(sketch, "E17.42.3.4", {"start": v(46, 38.54) * mm, "end": v(50, 38.54) * mm});
            skLineSegment(sketch, "E18.0.0.5", {"start": v(2, 35.5) * mm, "end": v(-2, 35.5) * mm});
            skLineSegment(sketch, "E18.3.0.5", {"start": v(-2, 35.5) * mm, "end": v(-4, 38.97) * mm});
            skCircle(sketch, "E18.6.0.5", {"center": v(0, 38.97) * mm, "radius": 3.46 * mm, "construction": true});
            skLineSegment(sketch, "E18.8.0.5", {"start": v(4, 38.97) * mm, "end": v(2, 35.5) * mm});
            skLineSegment(sketch, "E18.11.0.5", {"start": v(8.75, 39.4) * mm, "end": v(4.75, 39.4) * mm});
            skLineSegment(sketch, "E18.14.0.5", {"start": v(0, 38.97) * mm, "end": v(6.75, 42.87) * mm, "construction": true});
            skLineSegment(sketch, "E18.17.0.5", {"start": v(-4, 38.97) * mm, "end": v(-2, 42.44) * mm});
            skLineSegment(sketch, "E18.20.0.5", {"start": v(2, 42.44) * mm, "end": v(4, 38.97) * mm});
            skCircle(sketch, "E18.23.0.5", {"center": v(6.75, 42.87) * mm, "radius": 3.46 * mm, "construction": true});
            skPoint(sketch, "E18.25.0.5", {"position": v(0, 42.44) * mm});
            skLineSegment(sketch, "E18.26.0.5", {"start": v(4.75, 39.4) * mm, "end": v(2.75, 42.87) * mm});
            skLineSegment(sketch, "E18.29.0.5", {"start": v(10.75, 42.87) * mm, "end": v(8.75, 39.4) * mm});
            skLineSegment(sketch, "E18.32.0.5", {"start": v(2.75, 42.87) * mm, "end": v(4.75, 46.33) * mm});
            skLineSegment(sketch, "E18.35.0.5", {"start": v(8.75, 46.33) * mm, "end": v(10.75, 42.87) * mm});
            skPoint(sketch, "E18.38.0.5", {"position": v(6.75, 46.33) * mm});
            skLineSegment(sketch, "E18.39.0.5", {"start": v(-2, 42.44) * mm, "end": v(2, 42.44) * mm});
            skLineSegment(sketch, "E18.42.0.5", {"start": v(4.75, 46.33) * mm, "end": v(8.75, 46.33) * mm});
            skLineSegment(sketch, "E18.0.1.5", {"start": v(15.75, 35.5) * mm, "end": v(11.75, 35.5) * mm});
            skLineSegment(sketch, "E18.3.1.5", {"start": v(11.75, 35.5) * mm, "end": v(9.75, 38.97) * mm});
            skCircle(sketch, "E18.6.1.5", {"center": v(13.75, 38.97) * mm, "radius": 3.46 * mm, "construction": true});
            skLineSegment(sketch, "E18.8.1.5", {"start": v(17.75, 38.97) * mm, "end": v(15.75, 35.5) * mm});
            skLineSegment(sketch, "E18.11.1.5", {"start": v(22.5, 39.4) * mm, "end": v(18.5, 39.4) * mm});
            skLineSegment(sketch, "E18.14.1.5", {"start": v(13.75, 38.97) * mm, "end": v(20.5, 42.87) * mm, "construction": true});
            skLineSegment(sketch, "E18.17.1.5", {"start": v(9.75, 38.97) * mm, "end": v(11.75, 42.44) * mm});
            skLineSegment(sketch, "E18.20.1.5", {"start": v(15.75, 42.44) * mm, "end": v(17.75, 38.97) * mm});
            skCircle(sketch, "E18.23.1.5", {"center": v(20.5, 42.87) * mm, "radius": 3.46 * mm, "construction": true});
            skPoint(sketch, "E18.25.1.5", {"position": v(13.75, 42.44) * mm});
            skLineSegment(sketch, "E18.26.1.5", {"start": v(18.5, 39.4) * mm, "end": v(16.5, 42.87) * mm});
            skLineSegment(sketch, "E18.29.1.5", {"start": v(24.5, 42.87) * mm, "end": v(22.5, 39.4) * mm});
            skLineSegment(sketch, "E18.32.1.5", {"start": v(16.5, 42.87) * mm, "end": v(18.5, 46.33) * mm});
            skLineSegment(sketch, "E18.35.1.5", {"start": v(22.5, 46.33) * mm, "end": v(24.5, 42.87) * mm});
            skPoint(sketch, "E18.38.1.5", {"position": v(20.5, 46.33) * mm});
            skLineSegment(sketch, "E18.39.1.5", {"start": v(11.75, 42.44) * mm, "end": v(15.75, 42.44) * mm});
            skLineSegment(sketch, "E18.42.1.5", {"start": v(18.5, 46.33) * mm, "end": v(22.5, 46.33) * mm});
            skLineSegment(sketch, "E18.0.2.5", {"start": v(29.5, 35.5) * mm, "end": v(25.5, 35.5) * mm});
            skLineSegment(sketch, "E18.3.2.5", {"start": v(25.5, 35.5) * mm, "end": v(23.5, 38.97) * mm});
            skCircle(sketch, "E18.6.2.5", {"center": v(27.5, 38.97) * mm, "radius": 3.46 * mm, "construction": true});
            skLineSegment(sketch, "E18.8.2.5", {"start": v(31.5, 38.97) * mm, "end": v(29.5, 35.5) * mm});
            skLineSegment(sketch, "E18.11.2.5", {"start": v(36.25, 39.4) * mm, "end": v(32.25, 39.4) * mm});
            skLineSegment(sketch, "E18.14.2.5", {"start": v(27.5, 38.97) * mm, "end": v(34.25, 42.87) * mm, "construction": true});
            skLineSegment(sketch, "E18.17.2.5", {"start": v(23.5, 38.97) * mm, "end": v(25.5, 42.44) * mm});
            skLineSegment(sketch, "E18.20.2.5", {"start": v(29.5, 42.44) * mm, "end": v(31.5, 38.97) * mm});
            skCircle(sketch, "E18.23.2.5", {"center": v(34.25, 42.87) * mm, "radius": 3.46 * mm, "construction": true});
            skPoint(sketch, "E18.25.2.5", {"position": v(27.5, 42.44) * mm});
            skLineSegment(sketch, "E18.26.2.5", {"start": v(32.25, 39.4) * mm, "end": v(30.25, 42.87) * mm});
            skLineSegment(sketch, "E18.29.2.5", {"start": v(38.25, 42.87) * mm, "end": v(36.25, 39.4) * mm});
            skLineSegment(sketch, "E18.32.2.5", {"start": v(30.25, 42.87) * mm, "end": v(32.25, 46.33) * mm});
            skLineSegment(sketch, "E18.35.2.5", {"start": v(36.25, 46.33) * mm, "end": v(38.25, 42.87) * mm});
            skPoint(sketch, "E18.38.2.5", {"position": v(34.25, 46.33) * mm});
            skLineSegment(sketch, "E18.39.2.5", {"start": v(25.5, 42.44) * mm, "end": v(29.5, 42.44) * mm});
            skLineSegment(sketch, "E18.42.2.5", {"start": v(32.25, 46.33) * mm, "end": v(36.25, 46.33) * mm});
            skLineSegment(sketch, "E18.0.3.5", {"start": v(43.25, 35.5) * mm, "end": v(39.25, 35.5) * mm});
            skLineSegment(sketch, "E18.3.3.5", {"start": v(39.25, 35.5) * mm, "end": v(37.25, 38.97) * mm});
            skCircle(sketch, "E18.6.3.5", {"center": v(41.25, 38.97) * mm, "radius": 3.46 * mm, "construction": true});
            skLineSegment(sketch, "E18.8.3.5", {"start": v(45.25, 38.97) * mm, "end": v(43.25, 35.5) * mm});
            skLineSegment(sketch, "E18.11.3.5", {"start": v(50, 39.4) * mm, "end": v(46, 39.4) * mm});
            skLineSegment(sketch, "E18.14.3.5", {"start": v(41.25, 38.97) * mm, "end": v(48, 42.87) * mm, "construction": true});
            skLineSegment(sketch, "E18.17.3.5", {"start": v(37.25, 38.97) * mm, "end": v(39.25, 42.44) * mm});
            skLineSegment(sketch, "E18.20.3.5", {"start": v(43.25, 42.44) * mm, "end": v(45.25, 38.97) * mm});
            skCircle(sketch, "E18.23.3.5", {"center": v(48, 42.87) * mm, "radius": 3.46 * mm, "construction": true});
            skPoint(sketch, "E18.25.3.5", {"position": v(41.25, 42.44) * mm});
            skLineSegment(sketch, "E18.26.3.5", {"start": v(46, 39.4) * mm, "end": v(44, 42.87) * mm});
            skLineSegment(sketch, "E18.29.3.5", {"start": v(52, 42.87) * mm, "end": v(50, 39.4) * mm});
            skLineSegment(sketch, "E18.32.3.5", {"start": v(44, 42.87) * mm, "end": v(46, 46.33) * mm});
            skLineSegment(sketch, "E18.35.3.5", {"start": v(50, 46.33) * mm, "end": v(52, 42.87) * mm});
            skPoint(sketch, "E18.38.3.5", {"position": v(48, 46.33) * mm});
            skLineSegment(sketch, "E18.39.3.5", {"start": v(39.25, 42.44) * mm, "end": v(43.25, 42.44) * mm});
            skLineSegment(sketch, "E18.42.3.5", {"start": v(46, 46.33) * mm, "end": v(50, 46.33) * mm});
            skSolve(sketch);
        }
        {
            var Q0;
            {var subQ35=sQuery(id+"F3.wireOp",EDGE,"E9.1");Q0=makeQuery(id+"F3.imprint","IMPRINT",FACE,{"disambiguationData":[TD([[makeQuery(id+"F3.imprint","IMPRINT",EDGE,{"derivedFrom":subQ35}),1.0]])]});}
            extrude(context, id + "F4", {"entities" : qUnion([Q0]), "depth" : 1.5 * mm});
        }
        {
            var Q0;
            Q0=makeQuery(id+"F4.opExtrude","SWEPT_BODY",BODY,{"disambiguationData":[OSD([sQuery(id+"F3.wireOp",EDGE,"E9.0"),sQuery(id+"F3.wireOp",EDGE,"E9.1"),sQuery(id+"F3.wireOp",EDGE,"E10.0"),sQuery(id+"F3.wireOp",EDGE,"E10.1"),sQuery(id+"F3.wireOp",EDGE,"E10.2"),sQuery(id+"F3.wireOp",EDGE,"E10.3"),sQuery(id+"F3.wireOp",EDGE,"E10.4"),sQuery(id+"F3.wireOp",EDGE,"E10.5"),sQuery(id+"F3.wireOp",EDGE,"E12.0.1.0"),sQuery(id+"F3.wireOp",EDGE,"E12.0.1.3"),sQuery(id+"F3.wireOp",EDGE,"E12.0.1.4"),sQuery(id+"F3.wireOp",EDGE,"E12.0.1.7"),sQuery(id+"F3.wireOp",EDGE,"E12.0.1.10"),sQuery(id+"F3.wireOp",EDGE,"E12.0.1.11"),sQuery(id+"F3.wireOp",EDGE,"E12.0.1.12"),sQuery(id+"F3.wireOp",EDGE,"E12.0.1.13"),sQuery(id+"F3.wireOp",EDGE,"E12.0.1.15"),sQuery(id+"F3.wireOp",EDGE,"E12.0.1.16"),sQuery(id+"F3.wireOp",EDGE,"E12.1.0.4"),sQuery(id+"F3.wireOp",EDGE,"E12.1.0.6"),sQuery(id+"F3.wireOp",EDGE,"E12.1.0.7"),sQuery(id+"F3.wireOp",EDGE,"E12.1.0.10"),sQuery(id+"F3.wireOp",EDGE,"E12.1.0.11"),sQuery(id+"F3.wireOp",EDGE,"E12.1.0.12"),sQuery(id+"F3.wireOp",EDGE,"E12.1.0.13"),sQuery(id+"F3.wireOp",EDGE,"E12.1.0.15"),sQuery(id+"F3.wireOp",EDGE,"E12.1.0.16"),sQuery(id+"F3.wireOp",EDGE,"E12.1.1.0"),sQuery(id+"F3.wireOp",EDGE,"E12.1.1.1"),sQuery(id+"F3.wireOp",EDGE,"E12.1.1.3"),sQuery(id+"F3.wireOp",EDGE,"E12.1.1.4"),sQuery(id+"F3.wireOp",EDGE,"E12.1.1.6"),sQuery(id+"F3.wireOp",EDGE,"E12.1.1.7"),sQuery(id+"F3.wireOp",EDGE,"E12.1.1.10"),sQuery(id+"F3.wireOp",EDGE,"E12.1.1.11"),sQuery(id+"F3.wireOp",EDGE,"E12.1.1.12"),sQuery(id+"F3.wireOp",EDGE,"E12.1.1.13"),sQuery(id+"F3.wireOp",EDGE,"E12.1.1.15"),sQuery(id+"F3.wireOp",EDGE,"E12.1.1.16"),sQuery(id+"F3.wireOp",EDGE,"E12.2.0.4"),sQuery(id+"F3.wireOp",EDGE,"E12.2.0.6"),sQuery(id+"F3.wireOp",EDGE,"E12.2.0.7"),sQuery(id+"F3.wireOp",EDGE,"E12.2.0.10"),sQuery(id+"F3.wireOp",EDGE,"E12.2.0.12"),sQuery(id+"F3.wireOp",EDGE,"E12.2.0.15"),sQuery(id+"F3.wireOp",EDGE,"E12.2.0.16"),sQuery(id+"F3.wireOp",EDGE,"E12.2.1.0"),sQuery(id+"F3.wireOp",EDGE,"E12.2.1.1"),sQuery(id+"F3.wireOp",EDGE,"E12.2.1.3"),sQuery(id+"F3.wireOp",EDGE,"E12.2.1.4"),sQuery(id+"F3.wireOp",EDGE,"E12.2.1.6"),sQuery(id+"F3.wireOp",EDGE,"E12.2.1.7"),sQuery(id+"F3.wireOp",EDGE,"E12.2.1.10"),sQuery(id+"F3.wireOp",EDGE,"E12.2.1.12"),sQuery(id+"F3.wireOp",EDGE,"E12.2.1.15"),sQuery(id+"F3.wireOp",EDGE,"32bd9c0f-3777-4f45-ac84-4afd4f1f7fb8"),sQuery(id+"F3.wireOp",EDGE,"E13"),sQuery(id+"F3.wireOp",EDGE,"5fca24fd-092c-48e8-badb-6d01f1b6c982"),sQuery(id+"F3.wireOp",EDGE,"E14.0.0.2"),sQuery(id+"F3.wireOp",EDGE,"E14.8.0.2"),sQuery(id+"F3.wireOp",EDGE,"E14.11.0.2"),sQuery(id+"F3.wireOp",EDGE,"E14.20.0.2"),sQuery(id+"F3.wireOp",EDGE,"E14.26.0.2"),sQuery(id+"F3.wireOp",EDGE,"E14.29.0.2"),sQuery(id+"F3.wireOp",EDGE,"E14.32.0.2"),sQuery(id+"F3.wireOp",EDGE,"E14.35.0.2"),sQuery(id+"F3.wireOp",EDGE,"E14.39.0.2"),sQuery(id+"F3.wireOp",EDGE,"E14.42.0.2"),sQuery(id+"F3.wireOp",EDGE,"E14.0.0.3"),sQuery(id+"F3.wireOp",EDGE,"E14.8.0.3"),sQuery(id+"F3.wireOp",EDGE,"E14.11.0.3"),sQuery(id+"F3.wireOp",EDGE,"E14.20.0.3"),sQuery(id+"F3.wireOp",EDGE,"E14.26.0.3"),sQuery(id+"F3.wireOp",EDGE,"E14.29.0.3"),sQuery(id+"F3.wireOp",EDGE,"E14.32.0.3"),sQuery(id+"F3.wireOp",EDGE,"E14.35.0.3"),sQuery(id+"F3.wireOp",EDGE,"E14.39.0.3"),sQuery(id+"F3.wireOp",EDGE,"E14.42.0.3"),sQuery(id+"F3.wireOp",EDGE,"E14.0.1.2"),sQuery(id+"F3.wireOp",EDGE,"E14.3.1.2"),sQuery(id+"F3.wireOp",EDGE,"E14.8.1.2"),sQuery(id+"F3.wireOp",EDGE,"E14.11.1.2"),sQuery(id+"F3.wireOp",EDGE,"E14.17.1.2"),sQuery(id+"F3.wireOp",EDGE,"E14.20.1.2"),sQuery(id+"F3.wireOp",EDGE,"E14.26.1.2"),sQuery(id+"F3.wireOp",EDGE,"E14.29.1.2"),sQuery(id+"F3.wireOp",EDGE,"E14.32.1.2"),sQuery(id+"F3.wireOp",EDGE,"E14.35.1.2"),sQuery(id+"F3.wireOp",EDGE,"E14.39.1.2"),sQuery(id+"F3.wireOp",EDGE,"E14.42.1.2"),sQuery(id+"F3.wireOp",EDGE,"E14.0.1.3"),sQuery(id+"F3.wireOp",EDGE,"E14.3.1.3"),sQuery(id+"F3.wireOp",EDGE,"E14.8.1.3"),sQuery(id+"F3.wireOp",EDGE,"E14.11.1.3"),sQuery(id+"F3.wireOp",EDGE,"E14.17.1.3"),sQuery(id+"F3.wireOp",EDGE,"E14.20.1.3"),sQuery(id+"F3.wireOp",EDGE,"E14.26.1.3"),sQuery(id+"F3.wireOp",EDGE,"E14.29.1.3"),sQuery(id+"F3.wireOp",EDGE,"E14.32.1.3"),sQuery(id+"F3.wireOp",EDGE,"E14.39.1.3"),sQuery(id+"F3.wireOp",EDGE,"E14.0.2.2"),sQuery(id+"F3.wireOp",EDGE,"E14.3.2.2"),sQuery(id+"F3.wireOp",EDGE,"E14.8.2.2"),sQuery(id+"F3.wireOp",EDGE,"E14.17.2.2"),sQuery(id+"F3.wireOp",EDGE,"E14.39.2.2"),sQuery(id+"F3.wireOp",EDGE,"E14.0.2.3"),sQuery(id+"F3.wireOp",EDGE,"E14.3.2.3"),sQuery(id+"F3.wireOp",EDGE,"E14.17.2.3"),sQuery(id+"F3.wireOp",EDGE,"E15.0.0.4"),sQuery(id+"F3.wireOp",EDGE,"E15.8.0.4"),sQuery(id+"F3.wireOp",EDGE,"E15.11.0.4"),sQuery(id+"F3.wireOp",EDGE,"E15.20.0.4"),sQuery(id+"F3.wireOp",EDGE,"E15.26.0.4"),sQuery(id+"F3.wireOp",EDGE,"E15.29.0.4"),sQuery(id+"F3.wireOp",EDGE,"E15.39.0.4"),sQuery(id+"F3.wireOp",EDGE,"E15.0.1.4"),sQuery(id+"F3.wireOp",EDGE,"E15.3.1.4"),sQuery(id+"F3.wireOp",EDGE,"E15.8.1.4"),sQuery(id+"F3.wireOp",EDGE,"E15.17.1.4")])]});
            var Q1;
            Q1=qCreatedBy(makeId("Top.planeOp"),FACE);
            mirror(context, id + "F5", {"entities" : qUnion([Q0]), "mirrorPlane" : qUnion([Q1])});
        }
        {
            var Q0;
            Q0=makeQuery(id+"F4.opExtrude","SWEPT_BODY",BODY,{"disambiguationData":[OSD([sQuery(id+"F3.wireOp",EDGE,"E9.0"),sQuery(id+"F3.wireOp",EDGE,"E9.1"),sQuery(id+"F3.wireOp",EDGE,"E10.0"),sQuery(id+"F3.wireOp",EDGE,"E10.1"),sQuery(id+"F3.wireOp",EDGE,"E10.2"),sQuery(id+"F3.wireOp",EDGE,"E10.3"),sQuery(id+"F3.wireOp",EDGE,"E10.4"),sQuery(id+"F3.wireOp",EDGE,"E10.5"),sQuery(id+"F3.wireOp",EDGE,"E12.0.1.0"),sQuery(id+"F3.wireOp",EDGE,"E12.0.1.3"),sQuery(id+"F3.wireOp",EDGE,"E12.0.1.4"),sQuery(id+"F3.wireOp",EDGE,"E12.0.1.7"),sQuery(id+"F3.wireOp",EDGE,"E12.0.1.10"),sQuery(id+"F3.wireOp",EDGE,"E12.0.1.11"),sQuery(id+"F3.wireOp",EDGE,"E12.0.1.12"),sQuery(id+"F3.wireOp",EDGE,"E12.0.1.13"),sQuery(id+"F3.wireOp",EDGE,"E12.0.1.15"),sQuery(id+"F3.wireOp",EDGE,"E12.0.1.16"),sQuery(id+"F3.wireOp",EDGE,"E12.1.0.4"),sQuery(id+"F3.wireOp",EDGE,"E12.1.0.6"),sQuery(id+"F3.wireOp",EDGE,"E12.1.0.7"),sQuery(id+"F3.wireOp",EDGE,"E12.1.0.10"),sQuery(id+"F3.wireOp",EDGE,"E12.1.0.11"),sQuery(id+"F3.wireOp",EDGE,"E12.1.0.12"),sQuery(id+"F3.wireOp",EDGE,"E12.1.0.13"),sQuery(id+"F3.wireOp",EDGE,"E12.1.0.15"),sQuery(id+"F3.wireOp",EDGE,"E12.1.0.16"),sQuery(id+"F3.wireOp",EDGE,"E12.1.1.0"),sQuery(id+"F3.wireOp",EDGE,"E12.1.1.1"),sQuery(id+"F3.wireOp",EDGE,"E12.1.1.3"),sQuery(id+"F3.wireOp",EDGE,"E12.1.1.4"),sQuery(id+"F3.wireOp",EDGE,"E12.1.1.6"),sQuery(id+"F3.wireOp",EDGE,"E12.1.1.7"),sQuery(id+"F3.wireOp",EDGE,"E12.1.1.10"),sQuery(id+"F3.wireOp",EDGE,"E12.1.1.11"),sQuery(id+"F3.wireOp",EDGE,"E12.1.1.12"),sQuery(id+"F3.wireOp",EDGE,"E12.1.1.13"),sQuery(id+"F3.wireOp",EDGE,"E12.1.1.15"),sQuery(id+"F3.wireOp",EDGE,"E12.1.1.16"),sQuery(id+"F3.wireOp",EDGE,"E12.2.0.4"),sQuery(id+"F3.wireOp",EDGE,"E12.2.0.6"),sQuery(id+"F3.wireOp",EDGE,"E12.2.0.7"),sQuery(id+"F3.wireOp",EDGE,"E12.2.0.10"),sQuery(id+"F3.wireOp",EDGE,"E12.2.0.12"),sQuery(id+"F3.wireOp",EDGE,"E12.2.0.15"),sQuery(id+"F3.wireOp",EDGE,"E12.2.0.16"),sQuery(id+"F3.wireOp",EDGE,"E12.2.1.0"),sQuery(id+"F3.wireOp",EDGE,"E12.2.1.1"),sQuery(id+"F3.wireOp",EDGE,"E12.2.1.3"),sQuery(id+"F3.wireOp",EDGE,"E12.2.1.4"),sQuery(id+"F3.wireOp",EDGE,"E12.2.1.6"),sQuery(id+"F3.wireOp",EDGE,"E12.2.1.7"),sQuery(id+"F3.wireOp",EDGE,"E12.2.1.10"),sQuery(id+"F3.wireOp",EDGE,"E12.2.1.12"),sQuery(id+"F3.wireOp",EDGE,"E12.2.1.15"),sQuery(id+"F3.wireOp",EDGE,"32bd9c0f-3777-4f45-ac84-4afd4f1f7fb8"),sQuery(id+"F3.wireOp",EDGE,"E13"),sQuery(id+"F3.wireOp",EDGE,"5fca24fd-092c-48e8-badb-6d01f1b6c982"),sQuery(id+"F3.wireOp",EDGE,"E14.0.0.2"),sQuery(id+"F3.wireOp",EDGE,"E14.8.0.2"),sQuery(id+"F3.wireOp",EDGE,"E14.11.0.2"),sQuery(id+"F3.wireOp",EDGE,"E14.20.0.2"),sQuery(id+"F3.wireOp",EDGE,"E14.26.0.2"),sQuery(id+"F3.wireOp",EDGE,"E14.29.0.2"),sQuery(id+"F3.wireOp",EDGE,"E14.32.0.2"),sQuery(id+"F3.wireOp",EDGE,"E14.35.0.2"),sQuery(id+"F3.wireOp",EDGE,"E14.39.0.2"),sQuery(id+"F3.wireOp",EDGE,"E14.42.0.2"),sQuery(id+"F3.wireOp",EDGE,"E14.0.0.3"),sQuery(id+"F3.wireOp",EDGE,"E14.8.0.3"),sQuery(id+"F3.wireOp",EDGE,"E14.11.0.3"),sQuery(id+"F3.wireOp",EDGE,"E14.20.0.3"),sQuery(id+"F3.wireOp",EDGE,"E14.26.0.3"),sQuery(id+"F3.wireOp",EDGE,"E14.29.0.3"),sQuery(id+"F3.wireOp",EDGE,"E14.32.0.3"),sQuery(id+"F3.wireOp",EDGE,"E14.35.0.3"),sQuery(id+"F3.wireOp",EDGE,"E14.39.0.3"),sQuery(id+"F3.wireOp",EDGE,"E14.42.0.3"),sQuery(id+"F3.wireOp",EDGE,"E14.0.1.2"),sQuery(id+"F3.wireOp",EDGE,"E14.3.1.2"),sQuery(id+"F3.wireOp",EDGE,"E14.8.1.2"),sQuery(id+"F3.wireOp",EDGE,"E14.11.1.2"),sQuery(id+"F3.wireOp",EDGE,"E14.17.1.2"),sQuery(id+"F3.wireOp",EDGE,"E14.20.1.2"),sQuery(id+"F3.wireOp",EDGE,"E14.26.1.2"),sQuery(id+"F3.wireOp",EDGE,"E14.29.1.2"),sQuery(id+"F3.wireOp",EDGE,"E14.32.1.2"),sQuery(id+"F3.wireOp",EDGE,"E14.35.1.2"),sQuery(id+"F3.wireOp",EDGE,"E14.39.1.2"),sQuery(id+"F3.wireOp",EDGE,"E14.42.1.2"),sQuery(id+"F3.wireOp",EDGE,"E14.0.1.3"),sQuery(id+"F3.wireOp",EDGE,"E14.3.1.3"),sQuery(id+"F3.wireOp",EDGE,"E14.8.1.3"),sQuery(id+"F3.wireOp",EDGE,"E14.11.1.3"),sQuery(id+"F3.wireOp",EDGE,"E14.17.1.3"),sQuery(id+"F3.wireOp",EDGE,"E14.20.1.3"),sQuery(id+"F3.wireOp",EDGE,"E14.26.1.3"),sQuery(id+"F3.wireOp",EDGE,"E14.29.1.3"),sQuery(id+"F3.wireOp",EDGE,"E14.32.1.3"),sQuery(id+"F3.wireOp",EDGE,"E14.39.1.3"),sQuery(id+"F3.wireOp",EDGE,"E14.0.2.2"),sQuery(id+"F3.wireOp",EDGE,"E14.3.2.2"),sQuery(id+"F3.wireOp",EDGE,"E14.8.2.2"),sQuery(id+"F3.wireOp",EDGE,"E14.17.2.2"),sQuery(id+"F3.wireOp",EDGE,"E14.39.2.2"),sQuery(id+"F3.wireOp",EDGE,"E14.0.2.3"),sQuery(id+"F3.wireOp",EDGE,"E14.3.2.3"),sQuery(id+"F3.wireOp",EDGE,"E14.17.2.3"),sQuery(id+"F3.wireOp",EDGE,"E15.0.0.4"),sQuery(id+"F3.wireOp",EDGE,"E15.8.0.4"),sQuery(id+"F3.wireOp",EDGE,"E15.11.0.4"),sQuery(id+"F3.wireOp",EDGE,"E15.20.0.4"),sQuery(id+"F3.wireOp",EDGE,"E15.26.0.4"),sQuery(id+"F3.wireOp",EDGE,"E15.29.0.4"),sQuery(id+"F3.wireOp",EDGE,"E15.39.0.4"),sQuery(id+"F3.wireOp",EDGE,"E15.0.1.4"),sQuery(id+"F3.wireOp",EDGE,"E15.3.1.4"),sQuery(id+"F3.wireOp",EDGE,"E15.8.1.4"),sQuery(id+"F3.wireOp",EDGE,"E15.17.1.4")])]});
            var Q1;
            Q1=makeQuery(id+"F5.opPattern","COPY",BODY,{"derivedFrom":makeQuery(id+"F4.opExtrude","SWEPT_BODY",BODY,{"disambiguationData":[OSD([sQuery(id+"F3.wireOp",EDGE,"E9.0"),sQuery(id+"F3.wireOp",EDGE,"E9.1"),sQuery(id+"F3.wireOp",EDGE,"E10.0"),sQuery(id+"F3.wireOp",EDGE,"E10.1"),sQuery(id+"F3.wireOp",EDGE,"E10.2"),sQuery(id+"F3.wireOp",EDGE,"E10.3"),sQuery(id+"F3.wireOp",EDGE,"E10.4"),sQuery(id+"F3.wireOp",EDGE,"E10.5"),sQuery(id+"F3.wireOp",EDGE,"E12.0.1.0"),sQuery(id+"F3.wireOp",EDGE,"E12.0.1.3"),sQuery(id+"F3.wireOp",EDGE,"E12.0.1.4"),sQuery(id+"F3.wireOp",EDGE,"E12.0.1.7"),sQuery(id+"F3.wireOp",EDGE,"E12.0.1.10"),sQuery(id+"F3.wireOp",EDGE,"E12.0.1.11"),sQuery(id+"F3.wireOp",EDGE,"E12.0.1.12"),sQuery(id+"F3.wireOp",EDGE,"E12.0.1.13"),sQuery(id+"F3.wireOp",EDGE,"E12.0.1.15"),sQuery(id+"F3.wireOp",EDGE,"E12.0.1.16"),sQuery(id+"F3.wireOp",EDGE,"E12.1.0.4"),sQuery(id+"F3.wireOp",EDGE,"E12.1.0.6"),sQuery(id+"F3.wireOp",EDGE,"E12.1.0.7"),sQuery(id+"F3.wireOp",EDGE,"E12.1.0.10"),sQuery(id+"F3.wireOp",EDGE,"E12.1.0.11"),sQuery(id+"F3.wireOp",EDGE,"E12.1.0.12"),sQuery(id+"F3.wireOp",EDGE,"E12.1.0.13"),sQuery(id+"F3.wireOp",EDGE,"E12.1.0.15"),sQuery(id+"F3.wireOp",EDGE,"E12.1.0.16"),sQuery(id+"F3.wireOp",EDGE,"E12.1.1.0"),sQuery(id+"F3.wireOp",EDGE,"E12.1.1.1"),sQuery(id+"F3.wireOp",EDGE,"E12.1.1.3"),sQuery(id+"F3.wireOp",EDGE,"E12.1.1.4"),sQuery(id+"F3.wireOp",EDGE,"E12.1.1.6"),sQuery(id+"F3.wireOp",EDGE,"E12.1.1.7"),sQuery(id+"F3.wireOp",EDGE,"E12.1.1.10"),sQuery(id+"F3.wireOp",EDGE,"E12.1.1.11"),sQuery(id+"F3.wireOp",EDGE,"E12.1.1.12"),sQuery(id+"F3.wireOp",EDGE,"E12.1.1.13"),sQuery(id+"F3.wireOp",EDGE,"E12.1.1.15"),sQuery(id+"F3.wireOp",EDGE,"E12.1.1.16"),sQuery(id+"F3.wireOp",EDGE,"E12.2.0.4"),sQuery(id+"F3.wireOp",EDGE,"E12.2.0.6"),sQuery(id+"F3.wireOp",EDGE,"E12.2.0.7"),sQuery(id+"F3.wireOp",EDGE,"E12.2.0.10"),sQuery(id+"F3.wireOp",EDGE,"E12.2.0.12"),sQuery(id+"F3.wireOp",EDGE,"E12.2.0.15"),sQuery(id+"F3.wireOp",EDGE,"E12.2.0.16"),sQuery(id+"F3.wireOp",EDGE,"E12.2.1.0"),sQuery(id+"F3.wireOp",EDGE,"E12.2.1.1"),sQuery(id+"F3.wireOp",EDGE,"E12.2.1.3"),sQuery(id+"F3.wireOp",EDGE,"E12.2.1.4"),sQuery(id+"F3.wireOp",EDGE,"E12.2.1.6"),sQuery(id+"F3.wireOp",EDGE,"E12.2.1.7"),sQuery(id+"F3.wireOp",EDGE,"E12.2.1.10"),sQuery(id+"F3.wireOp",EDGE,"E12.2.1.12"),sQuery(id+"F3.wireOp",EDGE,"E12.2.1.15"),sQuery(id+"F3.wireOp",EDGE,"32bd9c0f-3777-4f45-ac84-4afd4f1f7fb8"),sQuery(id+"F3.wireOp",EDGE,"E13"),sQuery(id+"F3.wireOp",EDGE,"5fca24fd-092c-48e8-badb-6d01f1b6c982"),sQuery(id+"F3.wireOp",EDGE,"E14.0.0.2"),sQuery(id+"F3.wireOp",EDGE,"E14.8.0.2"),sQuery(id+"F3.wireOp",EDGE,"E14.11.0.2"),sQuery(id+"F3.wireOp",EDGE,"E14.20.0.2"),sQuery(id+"F3.wireOp",EDGE,"E14.26.0.2"),sQuery(id+"F3.wireOp",EDGE,"E14.29.0.2"),sQuery(id+"F3.wireOp",EDGE,"E14.32.0.2"),sQuery(id+"F3.wireOp",EDGE,"E14.35.0.2"),sQuery(id+"F3.wireOp",EDGE,"E14.39.0.2"),sQuery(id+"F3.wireOp",EDGE,"E14.42.0.2"),sQuery(id+"F3.wireOp",EDGE,"E14.0.0.3"),sQuery(id+"F3.wireOp",EDGE,"E14.8.0.3"),sQuery(id+"F3.wireOp",EDGE,"E14.11.0.3"),sQuery(id+"F3.wireOp",EDGE,"E14.20.0.3"),sQuery(id+"F3.wireOp",EDGE,"E14.26.0.3"),sQuery(id+"F3.wireOp",EDGE,"E14.29.0.3"),sQuery(id+"F3.wireOp",EDGE,"E14.32.0.3"),sQuery(id+"F3.wireOp",EDGE,"E14.35.0.3"),sQuery(id+"F3.wireOp",EDGE,"E14.39.0.3"),sQuery(id+"F3.wireOp",EDGE,"E14.42.0.3"),sQuery(id+"F3.wireOp",EDGE,"E14.0.1.2"),sQuery(id+"F3.wireOp",EDGE,"E14.3.1.2"),sQuery(id+"F3.wireOp",EDGE,"E14.8.1.2"),sQuery(id+"F3.wireOp",EDGE,"E14.11.1.2"),sQuery(id+"F3.wireOp",EDGE,"E14.17.1.2"),sQuery(id+"F3.wireOp",EDGE,"E14.20.1.2"),sQuery(id+"F3.wireOp",EDGE,"E14.26.1.2"),sQuery(id+"F3.wireOp",EDGE,"E14.29.1.2"),sQuery(id+"F3.wireOp",EDGE,"E14.32.1.2"),sQuery(id+"F3.wireOp",EDGE,"E14.35.1.2"),sQuery(id+"F3.wireOp",EDGE,"E14.39.1.2"),sQuery(id+"F3.wireOp",EDGE,"E14.42.1.2"),sQuery(id+"F3.wireOp",EDGE,"E14.0.1.3"),sQuery(id+"F3.wireOp",EDGE,"E14.3.1.3"),sQuery(id+"F3.wireOp",EDGE,"E14.8.1.3"),sQuery(id+"F3.wireOp",EDGE,"E14.11.1.3"),sQuery(id+"F3.wireOp",EDGE,"E14.17.1.3"),sQuery(id+"F3.wireOp",EDGE,"E14.20.1.3"),sQuery(id+"F3.wireOp",EDGE,"E14.26.1.3"),sQuery(id+"F3.wireOp",EDGE,"E14.29.1.3"),sQuery(id+"F3.wireOp",EDGE,"E14.32.1.3"),sQuery(id+"F3.wireOp",EDGE,"E14.39.1.3"),sQuery(id+"F3.wireOp",EDGE,"E14.0.2.2"),sQuery(id+"F3.wireOp",EDGE,"E14.3.2.2"),sQuery(id+"F3.wireOp",EDGE,"E14.8.2.2"),sQuery(id+"F3.wireOp",EDGE,"E14.17.2.2"),sQuery(id+"F3.wireOp",EDGE,"E14.39.2.2"),sQuery(id+"F3.wireOp",EDGE,"E14.0.2.3"),sQuery(id+"F3.wireOp",EDGE,"E14.3.2.3"),sQuery(id+"F3.wireOp",EDGE,"E14.17.2.3"),sQuery(id+"F3.wireOp",EDGE,"E15.0.0.4"),sQuery(id+"F3.wireOp",EDGE,"E15.8.0.4"),sQuery(id+"F3.wireOp",EDGE,"E15.11.0.4"),sQuery(id+"F3.wireOp",EDGE,"E15.20.0.4"),sQuery(id+"F3.wireOp",EDGE,"E15.26.0.4"),sQuery(id+"F3.wireOp",EDGE,"E15.29.0.4"),sQuery(id+"F3.wireOp",EDGE,"E15.39.0.4"),sQuery(id+"F3.wireOp",EDGE,"E15.0.1.4"),sQuery(id+"F3.wireOp",EDGE,"E15.3.1.4"),sQuery(id+"F3.wireOp",EDGE,"E15.8.1.4"),sQuery(id+"F3.wireOp",EDGE,"E15.17.1.4")])]}),"instanceName":"1"});
            var Q2;
            Q2=qCreatedBy(makeId("Right.planeOp"),FACE);
            mirror(context, id + "F6", {"entities" : qUnion([Q0, Q1]), "mirrorPlane" : qUnion([Q2])});
        }
    });
